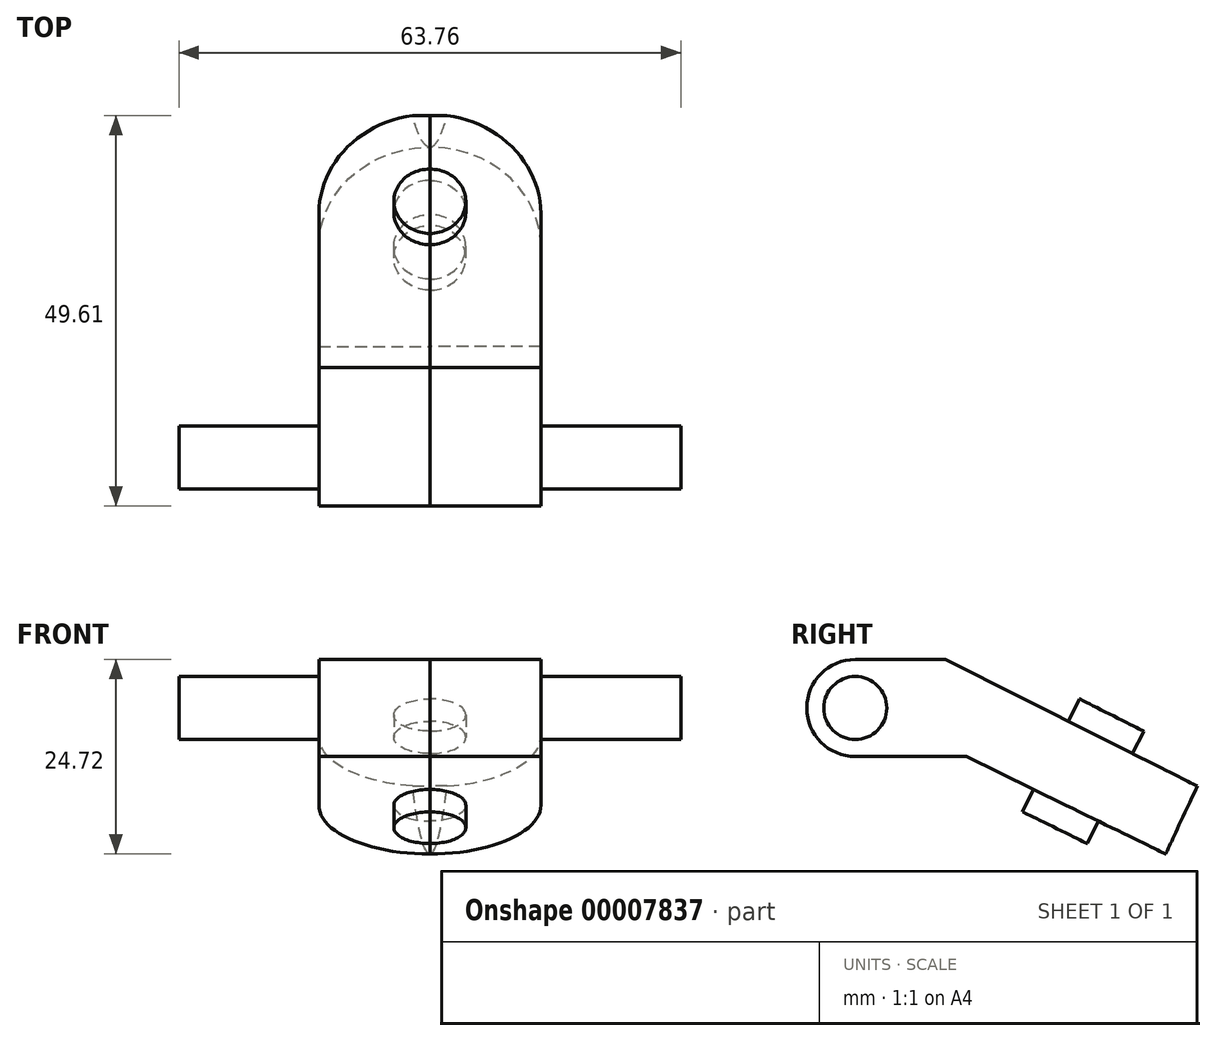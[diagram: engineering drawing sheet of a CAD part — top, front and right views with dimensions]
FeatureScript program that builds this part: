
annotation { "Feature Type Name" : "Feature", "Feature Type Description" : "" }
export const myFeature = defineFeature(function(context is Context, id is Id, definition is map)
    precondition{}
    {
        {
            var Q0;
            Q0=qCreatedBy(makeId("Right.planeOp"),FACE);
            var sketch = newSketch(context, id + "F0", { "sketchPlane" : qUnion([Q0])});
            skLineSegment(sketch, "E0.bottom", {"start": v(-12.68, -8.37) * mm, "end": v(-1.25, -8.37) * mm});
            skLineSegment(sketch, "E0.top", {"start": v(-12.68, -20.7) * mm, "end": v(1.42, -20.7) * mm});
            skLineSegment(sketch, "E0.left", {"start": v(-12.68, -8.37) * mm, "end": v(-12.68, -20.7) * mm});
            skLineSegment(sketch, "E0.right", {"start": v(-1.25, -8.37) * mm, "end": v(1.42, -20.7) * mm});
            skArc(sketch, "E1", {"start": v(-12.68, -8.37) * mm, "mid": v(-18.84, -14.53) * mm, "end": v(-12.68, -20.7) * mm});
            skLineSegment(sketch, "E2", {"start": v(1.42, -20.7) * mm, "end": v(26.74, -33.09) * mm});
            skLineSegment(sketch, "E3", {"start": v(26.74, -33.09) * mm, "end": v(30.77, -24.46) * mm});
            skLineSegment(sketch, "E4", {"start": v(30.77, -24.46) * mm, "end": v(-1.25, -8.37) * mm});
            skSolve(sketch);
        }
        {
            var Q0;
            Q0 = qSketchRegion(id + "F0", true);
            extrude(context, id + "F1", {"entities" : qUnion([Q0]), "oppositeDirection" : true, "depth" : 14.1 * mm});
        }
        {
            var Q0;
            Q0=makeQuery(id+"F1.opExtrude","CAP_FACE",FACE,{"disambiguationData":[OSD([sQuery(id+"F0.wireOp",EDGE,"E0.bottom"),sQuery(id+"F0.wireOp",EDGE,"E0.top"),sQuery(id+"F0.wireOp",EDGE,"E1"),sQuery(id+"F0.wireOp",EDGE,"E2"),sQuery(id+"F0.wireOp",EDGE,"E3"),sQuery(id+"F0.wireOp",EDGE,"E4")])],"isStart":false});
            var sketch = newSketch(context, id + "F2", { "sketchPlane" : qUnion([Q0])});
            skLineSegment(sketch, "E5", {"start": v(12.68, -20.7) * mm, "end": v(12.68, -8.37) * mm, "construction": true});
            skCircle(sketch, "E6", {"center": v(12.68, -14.53) * mm, "radius": 4 * mm});
            skSolve(sketch);
        }
        {
            var Q0;
            Q0=makeQuery(id+"F2.imprint","IMPRINT",FACE,{"disambiguationData":[TD([[makeQuery(id+"F2.imprint","IMPRINT",EDGE,{"derivedFrom":sQuery(id+"F2.wireOp",EDGE,"E6")}),1.0]])]});
            extrude(context, id + "F3", {"entities" : qUnion([Q0]), "operationType" : NewBodyOperationType.ADD, "depth" : 17.78 * mm});
        }
        {
            var Q0;
            Q0=makeQuery(id+"F1.opExtrude","SWEPT_FACE",FACE,{"disambiguationData":[OSD([sQuery(id+"F0.wireOp",EDGE,"E2")])]});
            var sketch = newSketch(context, id + "F4", { "sketchPlane" : qUnion([Q0])});
            skLineSegment(sketch, "E7.0", {"start": v(-14.1, -10.37) * mm, "end": v(-14.1, -24.47) * mm});
            skPoint(sketch, "E7.2", {"position": v(0, -38.57) * mm});
            skArc(sketch, "E8", {"start": v(-14.1, -24.47) * mm, "mid": v(-9.97, -34.44) * mm, "end": v(0, -38.57) * mm});
            skPoint(sketch, "E7.1.end.orphan", {"position": v(0, -38.57) * mm});
            skPoint(sketch, "E9.orphan", {"position": v(-14.1, -38.57) * mm});
            skSolve(sketch);
        }
        {
            var Q0;
            {var subQ2=sQuery(id+"F4.wireOp",EDGE,"E8");Q0=makeQuery(id+"F4.imprint","IMPRINT",FACE,{"disambiguationData":[TD([[makeQuery(id+"F4.imprint","IMPRINT",EDGE,{"derivedFrom":subQ2}),-1.0]])]});}
            extrude(context, id + "F5", {"entities" : qUnion([Q0]), "operationType" : NewBodyOperationType.REMOVE, "oppositeDirection" : true, "depth" : 25.4 * mm});
        }
        {
            var Q0;
            Q0=makeQuery(id+"F1.opExtrude","SWEPT_FACE",FACE,{"disambiguationData":[OSD([sQuery(id+"F0.wireOp",EDGE,"E2")])]});
            var sketch = newSketch(context, id + "F6", { "sketchPlane" : qUnion([Q0])});
            skArc(sketch, "E10", {"start": v(0, -19.9) * mm, "mid": v(-4.57, -24.47) * mm, "end": v(0, -29.04) * mm});
            skLineSegment(sketch, "E11.0", {"start": v(0, -10.37) * mm, "end": v(0, -38.57) * mm, "construction": true});
            skSolve(sketch);
        }
        {
            var Q0;
            {var subQ1=sQuery(id+"F6.wireOp",EDGE,"E10");Q0=makeQuery(id+"F6.imprint","IMPRINT",FACE,{"disambiguationData":[TD([[makeQuery(id+"F6.imprint","IMPRINT",EDGE,{"derivedFrom":subQ1}),1.0]])]});}
            extrude(context, id + "F7", {"entities" : qUnion([Q0]), "operationType" : NewBodyOperationType.ADD, "depth" : 3.17 * mm});
        }
        {
            var Q0;
            Q0=makeQuery(id+"F1.opExtrude","SWEPT_FACE",FACE,{"disambiguationData":[OSD([sQuery(id+"F0.wireOp",EDGE,"E4")])]});
            var sketch = newSketch(context, id + "F8", { "sketchPlane" : qUnion([Q0])});
            skLineSegment(sketch, "E12.0", {"start": v(0, 20.11) * mm, "end": v(0, 29.26) * mm});
            skArc(sketch, "E13", {"start": v(0, 29.26) * mm, "mid": v(-4.57, 24.68) * mm, "end": v(0, 20.11) * mm});
            skSolve(sketch);
        }
        {
            var Q0;
            Q0=makeQuery(id+"F8.imprint","IMPRINT",FACE,{"disambiguationData":[TD([[makeQuery(id+"F8.imprint","IMPRINT",EDGE,{"derivedFrom":sQuery(id+"F8.wireOp",EDGE,"E12.0")}),-1.0]])]});
            extrude(context, id + "F9", {"entities" : qUnion([Q0]), "operationType" : NewBodyOperationType.ADD, "depth" : 3.17 * mm});
        }
        {
            var Q0;
            Q0=makeQuery(id+"F1.opExtrude","SWEPT_BODY",BODY,{"disambiguationData":[OSD([sQuery(id+"F0.wireOp",EDGE,"E0.bottom"),sQuery(id+"F0.wireOp",EDGE,"E0.top"),sQuery(id+"F0.wireOp",EDGE,"E1"),sQuery(id+"F0.wireOp",EDGE,"E2"),sQuery(id+"F0.wireOp",EDGE,"E3"),sQuery(id+"F0.wireOp",EDGE,"E4")])]});
            var Q1;
            {var subQ0=sQuery(id+"F0.wireOp",EDGE,"E2");Q1=makeQuery(id+"F9.boolean.opBoolean","MERGE",FACE,{"derivedFrom":[makeQuery(id+"F7.boolean.opBoolean","MERGE",FACE,{"derivedFrom":[makeQuery(id+"F1.opExtrude","CAP_FACE",FACE,{"disambiguationData":[OSD([sQuery(id+"F0.wireOp",EDGE,"E0.bottom"),sQuery(id+"F0.wireOp",EDGE,"E0.top"),sQuery(id+"F0.wireOp",EDGE,"E1"),subQ0,sQuery(id+"F0.wireOp",EDGE,"E3"),sQuery(id+"F0.wireOp",EDGE,"E4")])],"isStart":true}),makeQuery(id+"F7.opExtrude","SWEPT_FACE",FACE,{"disambiguationData":[OSD([subQ0])]})]}),makeQuery(id+"F9.opExtrude","SWEPT_FACE",FACE,{"disambiguationData":[OSD([sQuery(id+"F8.wireOp",EDGE,"E12.0")])]})]});}
            mirror(context, id + "F10", {"entities" : qUnion([Q0]), "mirrorPlane" : qUnion([Q1])});
        }
    });
